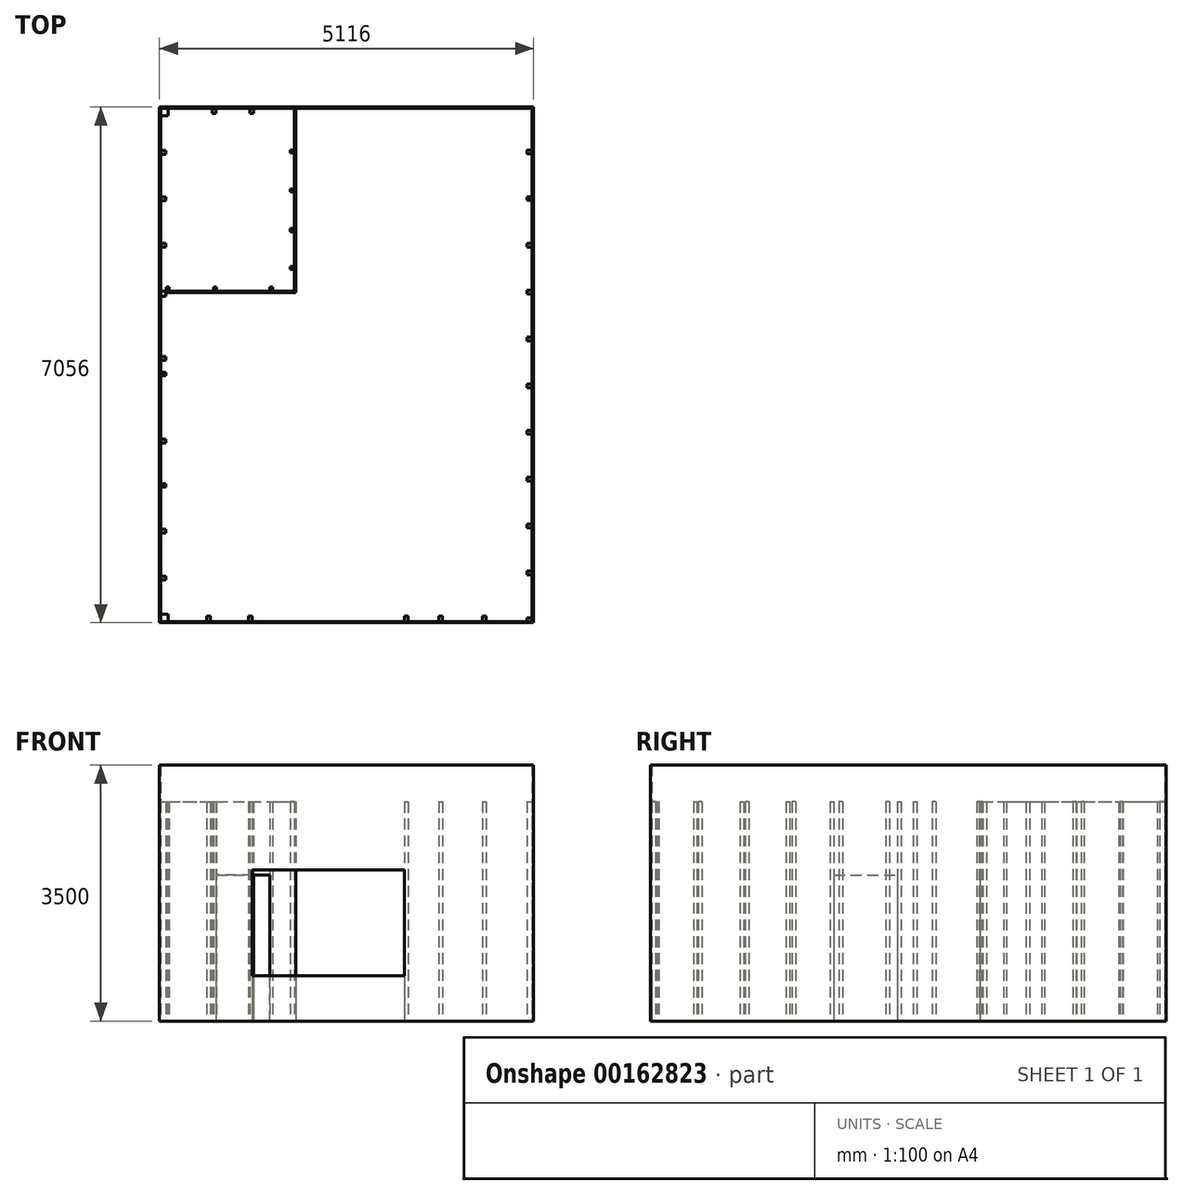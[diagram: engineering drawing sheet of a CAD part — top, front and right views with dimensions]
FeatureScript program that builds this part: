
annotation { "Feature Type Name" : "Feature", "Feature Type Description" : "" }
export const myFeature = defineFeature(function(context is Context, id is Id, definition is map)
    precondition{}
    {
        {
            assignVariable(context, id + "F0", {"name" : "Wys_zewnetrznych", "anyValue" : 3500});
        }
        {
            assignVariable(context, id + "F1", {"name" : "wys_parter", "anyValue" : 3000});
        }
        {
            var Q0;
            Q0=qCreatedBy(makeId("Top.planeOp"),FACE);
            var sketch = newSketch(context, id + "F2", { "sketchPlane" : qUnion([Q0])});
            skLineSegment(sketch, "E0", {"start": v(0, 0) * mm, "end": v(5080, 0) * mm});
            skLineSegment(sketch, "E1", {"start": v(0, 0) * mm, "end": v(0, 4500) * mm});
            skLineSegment(sketch, "E2", {"start": v(0, 4500) * mm, "end": v(1830, 4500) * mm});
            skLineSegment(sketch, "E3", {"start": v(1830, 4500) * mm, "end": v(1830, 7020) * mm});
            skLineSegment(sketch, "E4", {"start": v(1830, 7020) * mm, "end": v(5080, 7020) * mm});
            skLineSegment(sketch, "E5", {"start": v(5080, 7020) * mm, "end": v(5080, 0) * mm});
            skLineSegment(sketch, "E6", {"start": v(0, 4500) * mm, "end": v(0, 7020) * mm});
            skLineSegment(sketch, "E7", {"start": v(0, 7020) * mm, "end": v(1830, 7020) * mm});
            skLineSegment(sketch, "E8.bottom", {"start": v(5080, 0) * mm, "end": v(5010, 0) * mm});
            skLineSegment(sketch, "E8.top", {"start": v(5080, 50) * mm, "end": v(5010, 50) * mm});
            skLineSegment(sketch, "E8.left", {"start": v(5080, 0) * mm, "end": v(5080, 50) * mm});
            skLineSegment(sketch, "E8.right", {"start": v(5010, 0) * mm, "end": v(5010, 50) * mm});
            skLineSegment(sketch, "E9.0.1.0", {"start": v(5010, 640) * mm, "end": v(5010, 690) * mm});
            skLineSegment(sketch, "E9.0.1.1", {"start": v(5080, 690) * mm, "end": v(5010, 690) * mm});
            skLineSegment(sketch, "E9.0.1.2", {"start": v(5080, 640) * mm, "end": v(5080, 690) * mm});
            skLineSegment(sketch, "E9.0.1.3", {"start": v(5080, 640) * mm, "end": v(5010, 640) * mm});
            skLineSegment(sketch, "E9.0.2.0", {"start": v(5010, 1280) * mm, "end": v(5010, 1330) * mm});
            skLineSegment(sketch, "E9.0.2.1", {"start": v(5080, 1330) * mm, "end": v(5010, 1330) * mm});
            skLineSegment(sketch, "E9.0.2.2", {"start": v(5080, 1280) * mm, "end": v(5080, 1330) * mm});
            skLineSegment(sketch, "E9.0.2.3", {"start": v(5080, 1280) * mm, "end": v(5010, 1280) * mm});
            skLineSegment(sketch, "E9.0.3.0", {"start": v(5010, 1920) * mm, "end": v(5010, 1970) * mm});
            skLineSegment(sketch, "E9.0.3.1", {"start": v(5080, 1970) * mm, "end": v(5010, 1970) * mm});
            skLineSegment(sketch, "E9.0.3.2", {"start": v(5080, 1920) * mm, "end": v(5080, 1970) * mm});
            skLineSegment(sketch, "E9.0.3.3", {"start": v(5080, 1920) * mm, "end": v(5010, 1920) * mm});
            skLineSegment(sketch, "E9.0.4.0", {"start": v(5010, 2560) * mm, "end": v(5010, 2610) * mm});
            skLineSegment(sketch, "E9.0.4.1", {"start": v(5080, 2610) * mm, "end": v(5010, 2610) * mm});
            skLineSegment(sketch, "E9.0.4.2", {"start": v(5080, 2560) * mm, "end": v(5080, 2610) * mm});
            skLineSegment(sketch, "E9.0.4.3", {"start": v(5080, 2560) * mm, "end": v(5010, 2560) * mm});
            skLineSegment(sketch, "E9.0.5.0", {"start": v(5010, 3200) * mm, "end": v(5010, 3250) * mm});
            skLineSegment(sketch, "E9.0.5.1", {"start": v(5080, 3250) * mm, "end": v(5010, 3250) * mm});
            skLineSegment(sketch, "E9.0.5.2", {"start": v(5080, 3200) * mm, "end": v(5080, 3250) * mm});
            skLineSegment(sketch, "E9.0.5.3", {"start": v(5080, 3200) * mm, "end": v(5010, 3200) * mm});
            skLineSegment(sketch, "E9.0.6.0", {"start": v(5010, 3840) * mm, "end": v(5010, 3890) * mm});
            skLineSegment(sketch, "E9.0.6.1", {"start": v(5080, 3890) * mm, "end": v(5010, 3890) * mm});
            skLineSegment(sketch, "E9.0.6.2", {"start": v(5080, 3840) * mm, "end": v(5080, 3890) * mm});
            skLineSegment(sketch, "E9.0.6.3", {"start": v(5080, 3840) * mm, "end": v(5010, 3840) * mm});
            skLineSegment(sketch, "E9.0.7.0", {"start": v(5010, 4480) * mm, "end": v(5010, 4530) * mm});
            skLineSegment(sketch, "E9.0.7.1", {"start": v(5080, 4530) * mm, "end": v(5010, 4530) * mm});
            skLineSegment(sketch, "E9.0.7.2", {"start": v(5080, 4480) * mm, "end": v(5080, 4530) * mm});
            skLineSegment(sketch, "E9.0.7.3", {"start": v(5080, 4480) * mm, "end": v(5010, 4480) * mm});
            skLineSegment(sketch, "E9.0.8.0", {"start": v(5010, 5120) * mm, "end": v(5010, 5170) * mm});
            skLineSegment(sketch, "E9.0.8.1", {"start": v(5080, 5170) * mm, "end": v(5010, 5170) * mm});
            skLineSegment(sketch, "E9.0.8.2", {"start": v(5080, 5120) * mm, "end": v(5080, 5170) * mm});
            skLineSegment(sketch, "E9.0.8.3", {"start": v(5080, 5120) * mm, "end": v(5010, 5120) * mm});
            skLineSegment(sketch, "E9.0.9.0", {"start": v(5010, 5760) * mm, "end": v(5010, 5810) * mm});
            skLineSegment(sketch, "E9.0.9.1", {"start": v(5080, 5810) * mm, "end": v(5010, 5810) * mm});
            skLineSegment(sketch, "E9.0.9.2", {"start": v(5080, 5760) * mm, "end": v(5080, 5810) * mm});
            skLineSegment(sketch, "E9.0.9.3", {"start": v(5080, 5760) * mm, "end": v(5010, 5760) * mm});
            skLineSegment(sketch, "E9.0.10.0", {"start": v(5010, 6400) * mm, "end": v(5010, 6450) * mm});
            skLineSegment(sketch, "E9.0.10.1", {"start": v(5080, 6450) * mm, "end": v(5010, 6450) * mm});
            skLineSegment(sketch, "E9.0.10.2", {"start": v(5080, 6400) * mm, "end": v(5080, 6450) * mm});
            skLineSegment(sketch, "E9.0.10.3", {"start": v(5080, 6400) * mm, "end": v(5010, 6400) * mm});
            skLineSegment(sketch, "E9.direction1", {"start": v(5010, 0) * mm, "end": v(4985, 0) * mm, "construction": true});
            skLineSegment(sketch, "E9.direction2", {"start": v(5010, 0) * mm, "end": v(5010, 640) * mm, "construction": true});
            skLineSegment(sketch, "E10.bottom", {"start": v(4400, 0) * mm, "end": v(4450, 0) * mm});
            skLineSegment(sketch, "E10.top", {"start": v(4400, 70) * mm, "end": v(4450, 70) * mm});
            skLineSegment(sketch, "E10.left", {"start": v(4400, 0) * mm, "end": v(4400, 70) * mm});
            skLineSegment(sketch, "E10.right", {"start": v(4450, 0) * mm, "end": v(4450, 70) * mm});
            skLineSegment(sketch, "E11.bottom", {"start": v(3805, 0) * mm, "end": v(3855, 0) * mm});
            skLineSegment(sketch, "E11.top", {"start": v(3805, 70) * mm, "end": v(3855, 70) * mm});
            skLineSegment(sketch, "E11.left", {"start": v(3805, 0) * mm, "end": v(3805, 70) * mm});
            skLineSegment(sketch, "E11.right", {"start": v(3855, 0) * mm, "end": v(3855, 70) * mm});
            skLineSegment(sketch, "E12.bottom", {"start": v(3335, 0) * mm, "end": v(3385, 0) * mm});
            skLineSegment(sketch, "E12.top", {"start": v(3335, 70) * mm, "end": v(3385, 70) * mm});
            skLineSegment(sketch, "E12.left", {"start": v(3335, 0) * mm, "end": v(3335, 70) * mm});
            skLineSegment(sketch, "E12.right", {"start": v(3385, 0) * mm, "end": v(3385, 70) * mm});
            skLineSegment(sketch, "E13.bottom", {"start": v(0, 0) * mm, "end": v(100, 0) * mm});
            skLineSegment(sketch, "E13.top", {"start": v(0, 100) * mm, "end": v(100, 100) * mm});
            skLineSegment(sketch, "E13.left", {"start": v(0, 0) * mm, "end": v(0, 100) * mm});
            skLineSegment(sketch, "E13.right", {"start": v(100, 0) * mm, "end": v(100, 100) * mm});
            skLineSegment(sketch, "E14.bottom", {"start": v(627, 0) * mm, "end": v(677, 0) * mm});
            skLineSegment(sketch, "E14.top", {"start": v(627, 70) * mm, "end": v(677, 70) * mm});
            skLineSegment(sketch, "E14.left", {"start": v(627, 0) * mm, "end": v(627, 70) * mm});
            skLineSegment(sketch, "E14.right", {"start": v(677, 0) * mm, "end": v(677, 70) * mm});
            skLineSegment(sketch, "E15.bottom", {"start": v(1199, 0) * mm, "end": v(1249, 0) * mm});
            skLineSegment(sketch, "E15.top", {"start": v(1199, 70) * mm, "end": v(1249, 70) * mm});
            skLineSegment(sketch, "E15.left", {"start": v(1199, 0) * mm, "end": v(1199, 70) * mm});
            skLineSegment(sketch, "E15.right", {"start": v(1249, 0) * mm, "end": v(1249, 70) * mm});
            skText(sketch, "E16", { "text": "okno 620mm od podlogi\nwysokosc ok 1450", "fontName": "OpenSans-Regular.ttf"});
            skLineSegment(sketch, "E17.bottom", {"start": v(0, 571) * mm, "end": v(70, 571) * mm});
            skLineSegment(sketch, "E17.top", {"start": v(0, 621) * mm, "end": v(70, 621) * mm});
            skLineSegment(sketch, "E17.left", {"start": v(0, 571) * mm, "end": v(0, 621) * mm});
            skLineSegment(sketch, "E17.right", {"start": v(70, 571) * mm, "end": v(70, 621) * mm});
            skLineSegment(sketch, "E18.bottom", {"start": v(0, 1261) * mm, "end": v(70, 1261) * mm});
            skLineSegment(sketch, "E18.top", {"start": v(0, 1211) * mm, "end": v(70, 1211) * mm});
            skLineSegment(sketch, "E18.left", {"start": v(0, 1261) * mm, "end": v(0, 1211) * mm});
            skLineSegment(sketch, "E18.right", {"start": v(70, 1261) * mm, "end": v(70, 1211) * mm});
            skLineSegment(sketch, "E19.bottom", {"start": v(0, 1886) * mm, "end": v(70, 1886) * mm});
            skLineSegment(sketch, "E19.top", {"start": v(0, 1836) * mm, "end": v(70, 1836) * mm});
            skLineSegment(sketch, "E19.left", {"start": v(0, 1886) * mm, "end": v(0, 1836) * mm});
            skLineSegment(sketch, "E19.right", {"start": v(70, 1886) * mm, "end": v(70, 1836) * mm});
            skLineSegment(sketch, "E20.bottom", {"start": v(0, 2491) * mm, "end": v(70, 2491) * mm});
            skLineSegment(sketch, "E20.top", {"start": v(0, 2441) * mm, "end": v(70, 2441) * mm});
            skLineSegment(sketch, "E20.left", {"start": v(0, 2491) * mm, "end": v(0, 2441) * mm});
            skLineSegment(sketch, "E20.right", {"start": v(70, 2491) * mm, "end": v(70, 2441) * mm});
            skLineSegment(sketch, "E21.bottom", {"start": v(0, 3360) * mm, "end": v(70, 3360) * mm});
            skLineSegment(sketch, "E21.top", {"start": v(0, 3410) * mm, "end": v(70, 3410) * mm});
            skLineSegment(sketch, "E21.left", {"start": v(0, 3360) * mm, "end": v(0, 3410) * mm});
            skLineSegment(sketch, "E21.right", {"start": v(70, 3360) * mm, "end": v(70, 3410) * mm});
            skLineSegment(sketch, "E22.bottom", {"start": v(0, 3575) * mm, "end": v(70, 3575) * mm});
            skLineSegment(sketch, "E22.top", {"start": v(0, 3625) * mm, "end": v(70, 3625) * mm});
            skLineSegment(sketch, "E22.left", {"start": v(0, 3575) * mm, "end": v(0, 3625) * mm});
            skLineSegment(sketch, "E22.right", {"start": v(70, 3575) * mm, "end": v(70, 3625) * mm});
            skLineSegment(sketch, "E23.bottom", {"start": v(0, 4500) * mm, "end": v(70, 4500) * mm});
            skLineSegment(sketch, "E23.top", {"start": v(0, 4450) * mm, "end": v(70, 4450) * mm});
            skLineSegment(sketch, "E23.left", {"start": v(0, 4500) * mm, "end": v(0, 4450) * mm});
            skLineSegment(sketch, "E23.right", {"start": v(70, 4500) * mm, "end": v(70, 4450) * mm});
            skLineSegment(sketch, "E24.bottom", {"start": v(75, 4518) * mm, "end": v(115, 4518) * mm});
            skLineSegment(sketch, "E24.top", {"start": v(75, 4578) * mm, "end": v(115, 4578) * mm});
            skLineSegment(sketch, "E24.left", {"start": v(75, 4518) * mm, "end": v(75, 4578) * mm});
            skLineSegment(sketch, "E24.right", {"start": v(115, 4518) * mm, "end": v(115, 4578) * mm});
            skLineSegment(sketch, "E25.bottom", {"start": v(723, 4518) * mm, "end": v(763, 4518) * mm});
            skLineSegment(sketch, "E25.top", {"start": v(723, 4578) * mm, "end": v(763, 4578) * mm});
            skLineSegment(sketch, "E25.left", {"start": v(723, 4518) * mm, "end": v(723, 4578) * mm});
            skLineSegment(sketch, "E25.right", {"start": v(763, 4518) * mm, "end": v(763, 4578) * mm});
            skLineSegment(sketch, "E26.bottom", {"start": v(1490, 4518) * mm, "end": v(1530, 4518) * mm});
            skLineSegment(sketch, "E26.top", {"start": v(1490, 4578) * mm, "end": v(1530, 4578) * mm});
            skLineSegment(sketch, "E26.left", {"start": v(1490, 4518) * mm, "end": v(1490, 4578) * mm});
            skLineSegment(sketch, "E26.right", {"start": v(1530, 4518) * mm, "end": v(1530, 4578) * mm});
            skLineSegment(sketch, "E27.top", {"start": v(1775, 4578) * mm, "end": v(1815, 4578) * mm});
            skLineSegment(sketch, "E27.left", {"start": v(1775, 4518) * mm, "end": v(1775, 4578) * mm});
            skLineSegment(sketch, "E27.right", {"start": v(1815, 4518) * mm, "end": v(1815, 4578) * mm});
            skLineSegment(sketch, "E28.bottom", {"start": v(1830, 4816) * mm, "end": v(1770, 4816) * mm});
            skLineSegment(sketch, "E28.top", {"start": v(1830, 4856) * mm, "end": v(1770, 4856) * mm});
            skLineSegment(sketch, "E28.left", {"start": v(1830, 4816) * mm, "end": v(1830, 4856) * mm});
            skLineSegment(sketch, "E28.right", {"start": v(1770, 4816) * mm, "end": v(1770, 4856) * mm});
            skLineSegment(sketch, "E29.bottom", {"start": v(1830, 5334) * mm, "end": v(1770, 5334) * mm});
            skLineSegment(sketch, "E29.top", {"start": v(1830, 5374) * mm, "end": v(1770, 5374) * mm});
            skLineSegment(sketch, "E29.left", {"start": v(1830, 5334) * mm, "end": v(1830, 5374) * mm});
            skLineSegment(sketch, "E29.right", {"start": v(1770, 5334) * mm, "end": v(1770, 5374) * mm});
            skLineSegment(sketch, "E30.bottom", {"start": v(1830, 5916) * mm, "end": v(1770, 5916) * mm});
            skLineSegment(sketch, "E30.top", {"start": v(1830, 5876) * mm, "end": v(1770, 5876) * mm});
            skLineSegment(sketch, "E30.left", {"start": v(1830, 5916) * mm, "end": v(1830, 5876) * mm});
            skLineSegment(sketch, "E30.right", {"start": v(1770, 5916) * mm, "end": v(1770, 5876) * mm});
            skLineSegment(sketch, "E31.bottom", {"start": v(1830, 6408) * mm, "end": v(1770, 6408) * mm});
            skLineSegment(sketch, "E31.top", {"start": v(1830, 6448) * mm, "end": v(1770, 6448) * mm});
            skLineSegment(sketch, "E31.left", {"start": v(1830, 6408) * mm, "end": v(1830, 6448) * mm});
            skLineSegment(sketch, "E31.right", {"start": v(1770, 6408) * mm, "end": v(1770, 6448) * mm});
            skLineSegment(sketch, "E32.bottom", {"start": v(0, 7020) * mm, "end": v(100, 7020) * mm});
            skLineSegment(sketch, "E32.top", {"start": v(0, 6920) * mm, "end": v(100, 6920) * mm});
            skLineSegment(sketch, "E32.left", {"start": v(0, 7020) * mm, "end": v(0, 6920) * mm});
            skLineSegment(sketch, "E32.right", {"start": v(100, 7020) * mm, "end": v(100, 6920) * mm});
            skLineSegment(sketch, "E33.bottom", {"start": v(704, 7020) * mm, "end": v(754, 7020) * mm});
            skLineSegment(sketch, "E33.top", {"start": v(704, 6950) * mm, "end": v(754, 6950) * mm});
            skLineSegment(sketch, "E33.left", {"start": v(704, 7020) * mm, "end": v(704, 6950) * mm});
            skLineSegment(sketch, "E33.right", {"start": v(754, 7020) * mm, "end": v(754, 6950) * mm});
            skLineSegment(sketch, "E34.bottom", {"start": v(1269, 7020) * mm, "end": v(1219, 7020) * mm});
            skLineSegment(sketch, "E34.top", {"start": v(1269, 6950) * mm, "end": v(1219, 6950) * mm});
            skLineSegment(sketch, "E34.left", {"start": v(1269, 7020) * mm, "end": v(1269, 6950) * mm});
            skLineSegment(sketch, "E34.right", {"start": v(1219, 7020) * mm, "end": v(1219, 6950) * mm});
            skLineSegment(sketch, "E35.bottom", {"start": v(0, 6442) * mm, "end": v(70, 6442) * mm});
            skLineSegment(sketch, "E35.top", {"start": v(0, 6392) * mm, "end": v(70, 6392) * mm});
            skLineSegment(sketch, "E35.left", {"start": v(0, 6442) * mm, "end": v(0, 6392) * mm});
            skLineSegment(sketch, "E35.right", {"start": v(70, 6442) * mm, "end": v(70, 6392) * mm});
            skLineSegment(sketch, "E36.bottom", {"start": v(0, 5759) * mm, "end": v(70, 5759) * mm});
            skLineSegment(sketch, "E36.top", {"start": v(0, 5809) * mm, "end": v(70, 5809) * mm});
            skLineSegment(sketch, "E36.left", {"start": v(0, 5759) * mm, "end": v(0, 5809) * mm});
            skLineSegment(sketch, "E36.right", {"start": v(70, 5759) * mm, "end": v(70, 5809) * mm});
            skLineSegment(sketch, "E37.bottom", {"start": v(0, 5120) * mm, "end": v(70, 5120) * mm});
            skLineSegment(sketch, "E37.top", {"start": v(0, 5170) * mm, "end": v(70, 5170) * mm});
            skLineSegment(sketch, "E37.left", {"start": v(0, 5120) * mm, "end": v(0, 5170) * mm});
            skLineSegment(sketch, "E37.right", {"start": v(70, 5120) * mm, "end": v(70, 5170) * mm});
            skLineSegment(sketch, "E38", {"start": v(1775, 4518) * mm, "end": v(1815, 4518) * mm});
            skPoint(sketch, "E38.startSnap0", {"position": v(1510, 4518) * mm});
            skPoint(sketch, "E39.orphan", {"position": v(1775, 4546.29) * mm});
            skPoint(sketch, "E40.orphan", {"position": v(1815, 4518) * mm});
            skPoint(sketch, "E41.orphan", {"position": v(1815, 4550.5) * mm});
            const initialGuessF2  = {"E16": [1.86616, -0.28119, 1, 0, 0.10051]};
            skSetInitialGuess(sketch, initialGuessF2);
            skSolve(sketch);
        }
        {
            var Q0;
            {var subQ39=sQuery(id+"F2.wireOp",EDGE,"E4");Q0=makeQuery(id+"F2.imprint","IMPRINT",FACE,{"disambiguationData":[TD([[makeQuery(id+"F2.imprint","IMPRINT",EDGE,{"derivedFrom":subQ39}),-1.0]])]});}
            var sketch = newSketch(context, id + "F3", { "sketchPlane" : qUnion([Q0])});
            skPoint(sketch, "E42.orphan", {"position": v(0, 7021.81) * mm});
            skLineSegment(sketch, "E43.0", {"start": v(0, 7020) * mm, "end": v(1830, 7020) * mm});
            skLineSegment(sketch, "E43.1", {"start": v(1830, 7020) * mm, "end": v(5080, 7020) * mm});
            skLineSegment(sketch, "E43.2", {"start": v(0, 4500) * mm, "end": v(0, 7020) * mm});
            skLineSegment(sketch, "E43.3", {"start": v(0, 0) * mm, "end": v(0, 4500) * mm});
            skLineSegment(sketch, "E43.4", {"start": v(0, 0) * mm, "end": v(5080, 0) * mm});
            skLineSegment(sketch, "E43.5", {"start": v(5080, 7020) * mm, "end": v(5080, 0) * mm});
            skLineSegment(sketch, "E44.0", {"start": v(-18, 7038) * mm, "end": v(1830, 7038) * mm});
            skLineSegment(sketch, "E44.1", {"start": v(5098, 7038) * mm, "end": v(5098, -18) * mm});
            skLineSegment(sketch, "E44.2", {"start": v(-18, -18) * mm, "end": v(5098, -18) * mm});
            skLineSegment(sketch, "E44.3", {"start": v(1830, 7038) * mm, "end": v(5098, 7038) * mm});
            skLineSegment(sketch, "E44.4", {"start": v(-18, -18) * mm, "end": v(-18, 4500) * mm});
            skLineSegment(sketch, "E44.5", {"start": v(-18, 4500) * mm, "end": v(-18, 7038) * mm});
            skSolve(sketch);
        }
        {
            var Q0;
            Q0 = qSketchRegion(id + "F3", true);
            extrude(context, id + "F4", {"entities" : qUnion([Q0]), "depth" : (getVariable(context, 'Wys_zewnetrznych')) * mm});
        }
        {
            var Q0;
            {var subQ39=sQuery(id+"F2.wireOp",EDGE,"E4");Q0=makeQuery(id+"F2.imprint","IMPRINT",FACE,{"disambiguationData":[TD([[makeQuery(id+"F2.imprint","IMPRINT",EDGE,{"derivedFrom":subQ39}),-1.0]])]});}
            var sketch = newSketch(context, id + "F5", { "sketchPlane" : qUnion([Q0])});
            skLineSegment(sketch, "E45.0", {"start": v(0, 4500) * mm, "end": v(1830, 4500) * mm});
            skLineSegment(sketch, "E45.1", {"start": v(1830, 4518) * mm, "end": v(1830, 7020) * mm});
            skLineSegment(sketch, "E46.0", {"start": v(0, 4518) * mm, "end": v(1830, 4518) * mm});
            skLineSegment(sketch, "E47", {"start": v(0, 4500) * mm, "end": v(0, 4518) * mm});
            skLineSegment(sketch, "E48.0", {"start": v(1848, 4500) * mm, "end": v(1848, 7020) * mm});
            skLineSegment(sketch, "E49", {"start": v(1830, 4500) * mm, "end": v(1848, 4500) * mm});
            skLineSegment(sketch, "E50", {"start": v(1830, 7020) * mm, "end": v(1848, 7020) * mm});
            skPoint(sketch, "E51.orphan", {"position": v(1830, 4500) * mm});
            skSolve(sketch);
        }
        {
            var Q0;
            Q0 = qSketchRegion(id + "F5", true);
            extrude(context, id + "F6", {"entities" : qUnion([Q0]), "operationType" : NewBodyOperationType.ADD, "depth" : (getVariable(context, 'wys_parter')) * mm});
        }
        {
            var Q0;
            {var subQ3=sQuery(id+"F2.wireOp",EDGE,"E23.top");Q0=makeQuery(id+"F2.imprint","IMPRINT",FACE,{"disambiguationData":[TD([[makeQuery(id+"F2.imprint","IMPRINT",EDGE,{"derivedFrom":subQ3}),1.0]])]});}
            var Q1;
            {var subQ0=sQuery(id+"F2.wireOp",EDGE,"E22.bottom");Q1=makeQuery(id+"F2.imprint","IMPRINT",FACE,{"disambiguationData":[TD([[makeQuery(id+"F2.imprint","IMPRINT",EDGE,{"derivedFrom":subQ0}),1.0]])]});}
            var Q2;
            {var subQ0=sQuery(id+"F2.wireOp",EDGE,"E21.bottom");Q2=makeQuery(id+"F2.imprint","IMPRINT",FACE,{"disambiguationData":[TD([[makeQuery(id+"F2.imprint","IMPRINT",EDGE,{"derivedFrom":subQ0}),1.0]])]});}
            var Q3;
            {var subQ0=sQuery(id+"F2.wireOp",EDGE,"E20.bottom");Q3=makeQuery(id+"F2.imprint","IMPRINT",FACE,{"disambiguationData":[TD([[makeQuery(id+"F2.imprint","IMPRINT",EDGE,{"derivedFrom":subQ0}),-1.0]])]});}
            var Q4;
            {var subQ0=sQuery(id+"F2.wireOp",EDGE,"E19.bottom");Q4=makeQuery(id+"F2.imprint","IMPRINT",FACE,{"disambiguationData":[TD([[makeQuery(id+"F2.imprint","IMPRINT",EDGE,{"derivedFrom":subQ0}),-1.0]])]});}
            var Q5;
            {var subQ0=sQuery(id+"F2.wireOp",EDGE,"E18.bottom");Q5=makeQuery(id+"F2.imprint","IMPRINT",FACE,{"disambiguationData":[TD([[makeQuery(id+"F2.imprint","IMPRINT",EDGE,{"derivedFrom":subQ0}),-1.0]])]});}
            var Q6;
            {var subQ0=sQuery(id+"F2.wireOp",EDGE,"E17.bottom");Q6=makeQuery(id+"F2.imprint","IMPRINT",FACE,{"disambiguationData":[TD([[makeQuery(id+"F2.imprint","IMPRINT",EDGE,{"derivedFrom":subQ0}),1.0]])]});}
            var Q7;
            {var subQ4=sQuery(id+"F2.wireOp",EDGE,"E13.top");Q7=makeQuery(id+"F2.imprint","IMPRINT",FACE,{"disambiguationData":[TD([[makeQuery(id+"F2.imprint","IMPRINT",EDGE,{"derivedFrom":subQ4}),-1.0]])]});}
            var Q8;
            Q8=makeQuery(id+"F2.imprint","IMPRINT",FACE,{"disambiguationData":[TD([[makeQuery(id+"F2.imprint","IMPRINT",EDGE,{"derivedFrom":sQuery(id+"F2.wireOp",EDGE,"E14.top")}),-1.0]])]});
            var Q9;
            Q9=makeQuery(id+"F2.imprint","IMPRINT",FACE,{"disambiguationData":[TD([[makeQuery(id+"F2.imprint","IMPRINT",EDGE,{"derivedFrom":sQuery(id+"F2.wireOp",EDGE,"E15.top")}),-1.0]])]});
            var Q10;
            Q10=makeQuery(id+"F2.imprint","IMPRINT",FACE,{"disambiguationData":[TD([[makeQuery(id+"F2.imprint","IMPRINT",EDGE,{"derivedFrom":sQuery(id+"F2.wireOp",EDGE,"E12.top")}),-1.0]])]});
            var Q11;
            Q11=makeQuery(id+"F2.imprint","IMPRINT",FACE,{"disambiguationData":[TD([[makeQuery(id+"F2.imprint","IMPRINT",EDGE,{"derivedFrom":sQuery(id+"F2.wireOp",EDGE,"E11.top")}),-1.0]])]});
            var Q12;
            Q12=makeQuery(id+"F2.imprint","IMPRINT",FACE,{"disambiguationData":[TD([[makeQuery(id+"F2.imprint","IMPRINT",EDGE,{"derivedFrom":sQuery(id+"F2.wireOp",EDGE,"E10.top")}),-1.0]])]});
            var Q13;
            {var subQ4=sQuery(id+"F2.wireOp",EDGE,"E8.top");Q13=makeQuery(id+"F2.imprint","IMPRINT",FACE,{"disambiguationData":[TD([[makeQuery(id+"F2.imprint","IMPRINT",EDGE,{"derivedFrom":subQ4}),1.0]])]});}
            var Q14;
            Q14=makeQuery(id+"F2.imprint","IMPRINT",FACE,{"disambiguationData":[TD([[makeQuery(id+"F2.imprint","IMPRINT",EDGE,{"derivedFrom":sQuery(id+"F2.wireOp",EDGE,"E9.0.1.0")}),-1.0]])]});
            var Q15;
            Q15=makeQuery(id+"F2.imprint","IMPRINT",FACE,{"disambiguationData":[TD([[makeQuery(id+"F2.imprint","IMPRINT",EDGE,{"derivedFrom":sQuery(id+"F2.wireOp",EDGE,"E9.0.2.0")}),-1.0]])]});
            var Q16;
            Q16=makeQuery(id+"F2.imprint","IMPRINT",FACE,{"disambiguationData":[TD([[makeQuery(id+"F2.imprint","IMPRINT",EDGE,{"derivedFrom":sQuery(id+"F2.wireOp",EDGE,"E9.0.3.0")}),-1.0]])]});
            var Q17;
            Q17=makeQuery(id+"F2.imprint","IMPRINT",FACE,{"disambiguationData":[TD([[makeQuery(id+"F2.imprint","IMPRINT",EDGE,{"derivedFrom":sQuery(id+"F2.wireOp",EDGE,"E9.0.4.0")}),-1.0]])]});
            var Q18;
            Q18=makeQuery(id+"F2.imprint","IMPRINT",FACE,{"disambiguationData":[TD([[makeQuery(id+"F2.imprint","IMPRINT",EDGE,{"derivedFrom":sQuery(id+"F2.wireOp",EDGE,"E9.0.5.0")}),-1.0]])]});
            var Q19;
            Q19=makeQuery(id+"F2.imprint","IMPRINT",FACE,{"disambiguationData":[TD([[makeQuery(id+"F2.imprint","IMPRINT",EDGE,{"derivedFrom":sQuery(id+"F2.wireOp",EDGE,"E9.0.6.0")}),-1.0]])]});
            var Q20;
            Q20=makeQuery(id+"F2.imprint","IMPRINT",FACE,{"disambiguationData":[TD([[makeQuery(id+"F2.imprint","IMPRINT",EDGE,{"derivedFrom":sQuery(id+"F2.wireOp",EDGE,"E9.0.7.0")}),-1.0]])]});
            var Q21;
            Q21=makeQuery(id+"F2.imprint","IMPRINT",FACE,{"disambiguationData":[TD([[makeQuery(id+"F2.imprint","IMPRINT",EDGE,{"derivedFrom":sQuery(id+"F2.wireOp",EDGE,"E9.0.8.0")}),-1.0]])]});
            var Q22;
            Q22=makeQuery(id+"F2.imprint","IMPRINT",FACE,{"disambiguationData":[TD([[makeQuery(id+"F2.imprint","IMPRINT",EDGE,{"derivedFrom":sQuery(id+"F2.wireOp",EDGE,"E9.0.9.0")}),-1.0]])]});
            var Q23;
            Q23=makeQuery(id+"F2.imprint","IMPRINT",FACE,{"disambiguationData":[TD([[makeQuery(id+"F2.imprint","IMPRINT",EDGE,{"derivedFrom":sQuery(id+"F2.wireOp",EDGE,"E9.0.10.0")}),-1.0]])]});
            var Q24;
            {var subQ0=sQuery(id+"F2.wireOp",EDGE,"E32.top");Q24=makeQuery(id+"F2.imprint","IMPRINT",FACE,{"disambiguationData":[TD([[makeQuery(id+"F2.imprint","IMPRINT",EDGE,{"derivedFrom":subQ0}),1.0]])]});}
            var Q25;
            Q25=makeQuery(id+"F2.imprint","IMPRINT",FACE,{"disambiguationData":[TD([[makeQuery(id+"F2.imprint","IMPRINT",EDGE,{"derivedFrom":sQuery(id+"F2.wireOp",EDGE,"E33.top")}),1.0]])]});
            var Q26;
            Q26=makeQuery(id+"F2.imprint","IMPRINT",FACE,{"disambiguationData":[TD([[makeQuery(id+"F2.imprint","IMPRINT",EDGE,{"derivedFrom":sQuery(id+"F2.wireOp",EDGE,"E34.top")}),-1.0]])]});
            var Q27;
            {var subQ2=sQuery(id+"F2.wireOp",EDGE,"E31.bottom");Q27=makeQuery(id+"F2.imprint","IMPRINT",FACE,{"disambiguationData":[TD([[makeQuery(id+"F2.imprint","IMPRINT",EDGE,{"derivedFrom":subQ2}),-1.0]])]});}
            var Q28;
            {var subQ0=sQuery(id+"F2.wireOp",EDGE,"E30.bottom");Q28=makeQuery(id+"F2.imprint","IMPRINT",FACE,{"disambiguationData":[TD([[makeQuery(id+"F2.imprint","IMPRINT",EDGE,{"derivedFrom":subQ0}),1.0]])]});}
            var Q29;
            {var subQ2=sQuery(id+"F2.wireOp",EDGE,"E29.bottom");Q29=makeQuery(id+"F2.imprint","IMPRINT",FACE,{"disambiguationData":[TD([[makeQuery(id+"F2.imprint","IMPRINT",EDGE,{"derivedFrom":subQ2}),-1.0]])]});}
            var Q30;
            {var subQ0=sQuery(id+"F2.wireOp",EDGE,"E28.bottom");Q30=makeQuery(id+"F2.imprint","IMPRINT",FACE,{"disambiguationData":[TD([[makeQuery(id+"F2.imprint","IMPRINT",EDGE,{"derivedFrom":subQ0}),-1.0]])]});}
            var Q31;
            {var subQ0=sQuery(id+"F2.wireOp",EDGE,"E35.bottom");Q31=makeQuery(id+"F2.imprint","IMPRINT",FACE,{"disambiguationData":[TD([[makeQuery(id+"F2.imprint","IMPRINT",EDGE,{"derivedFrom":subQ0}),-1.0]])]});}
            var Q32;
            {var subQ0=sQuery(id+"F2.wireOp",EDGE,"E36.bottom");Q32=makeQuery(id+"F2.imprint","IMPRINT",FACE,{"disambiguationData":[TD([[makeQuery(id+"F2.imprint","IMPRINT",EDGE,{"derivedFrom":subQ0}),1.0]])]});}
            var Q33;
            {var subQ2=sQuery(id+"F2.wireOp",EDGE,"E37.bottom");Q33=makeQuery(id+"F2.imprint","IMPRINT",FACE,{"disambiguationData":[TD([[makeQuery(id+"F2.imprint","IMPRINT",EDGE,{"derivedFrom":subQ2}),1.0]])]});}
            var Q34;
            Q34=makeQuery(id+"F2.imprint","IMPRINT",FACE,{"disambiguationData":[TD([[makeQuery(id+"F2.imprint","IMPRINT",EDGE,{"derivedFrom":sQuery(id+"F2.wireOp",EDGE,"E24.bottom")}),1.0]])]});
            var Q35;
            Q35=makeQuery(id+"F2.imprint","IMPRINT",FACE,{"disambiguationData":[TD([[makeQuery(id+"F2.imprint","IMPRINT",EDGE,{"derivedFrom":sQuery(id+"F2.wireOp",EDGE,"E25.bottom")}),1.0]])]});
            var Q36;
            Q36=makeQuery(id+"F2.imprint","IMPRINT",FACE,{"disambiguationData":[TD([[makeQuery(id+"F2.imprint","IMPRINT",EDGE,{"derivedFrom":sQuery(id+"F2.wireOp",EDGE,"E26.bottom")}),1.0]])]});
            var Q37;
            Q37=makeQuery(id+"F2.imprint","IMPRINT",FACE,{"disambiguationData":[TD([[makeQuery(id+"F2.imprint","IMPRINT",EDGE,{"derivedFrom":sQuery(id+"F2.wireOp",EDGE,"E27.bottom")}),1.0]])]});
            extrude(context, id + "F7", {"entities" : qUnion([Q0, Q1, Q2, Q3, Q4, Q5, Q6, Q7, Q8, Q9, Q10, Q11, Q12, Q13, Q14, Q15, Q16, Q17, Q18, Q19, Q20, Q21, Q22, Q23, Q24, Q25, Q26, Q27, Q28, Q29, Q30, Q31, Q32, Q33, Q34, Q35, Q36, Q37]), "operationType" : NewBodyOperationType.ADD, "depth" : (getVariable(context, 'wys_parter')) * mm});
        }
        {
            var Q0;
            Q0=makeQuery(id+"F4.opExtrude","SWEPT_FACE",FACE,{"disambiguationData":[OSD([sQuery(id+"F3.wireOp",EDGE,"E44.2")])]});
            var sketch = newSketch(context, id + "F8", { "sketchPlane" : qUnion([Q0])});
            skLineSegment(sketch, "E52.0", {"start": v(1249, 2070) * mm, "end": v(1249, 620) * mm});
            skLineSegment(sketch, "E52.1", {"start": v(3335, 2070) * mm, "end": v(3335, 620) * mm});
            skLineSegment(sketch, "E53", {"start": v(1249, 620) * mm, "end": v(3335, 620) * mm});
            skLineSegment(sketch, "E54", {"start": v(1249, 2070) * mm, "end": v(3335, 2070) * mm});
            skSolve(sketch);
        }
        {
            var Q0;
            Q0=makeQuery(id+"F8.imprint","IMPRINT",FACE,{"disambiguationData":[TD([[makeQuery(id+"F8.imprint","IMPRINT",EDGE,{"derivedFrom":sQuery(id+"F8.wireOp",EDGE,"E52.0")}),1.0]])]});
            extrude(context, id + "F9", {"entities" : qUnion([Q0]), "operationType" : NewBodyOperationType.REMOVE, "endBound" : BoundingType.UP_TO_NEXT, "oppositeDirection" : true, "depth" : 25 * mm});
        }
        {
            var Q0;
            Q0=makeQuery(id+"F4.opExtrude","SWEPT_FACE",FACE,{"disambiguationData":[OSD([sQuery(id+"F3.wireOp",EDGE,"E43.2"),sQuery(id+"F3.wireOp",EDGE,"E43.3")])]});
            var sketch = newSketch(context, id + "F10", { "sketchPlane" : qUnion([Q0])});
            skLineSegment(sketch, "E55.0", {"start": v(3360, 2000) * mm, "end": v(3360, 0) * mm});
            skLineSegment(sketch, "E55.1", {"start": v(2491, 2000) * mm, "end": v(2491, 0) * mm});
            skLineSegment(sketch, "E56", {"start": v(2491, 2000) * mm, "end": v(3360, 2000) * mm});
            skLineSegment(sketch, "E57", {"start": v(2491, 0) * mm, "end": v(3360, 0) * mm});
            skSolve(sketch);
        }
        {
            var Q0;
            Q0=makeQuery(id+"F10.imprint","IMPRINT",FACE,{"disambiguationData":[TD([[makeQuery(id+"F10.imprint","IMPRINT",EDGE,{"derivedFrom":sQuery(id+"F10.wireOp",EDGE,"E55.0")}),-1.0]])]});
            extrude(context, id + "F11", {"entities" : qUnion([Q0]), "operationType" : NewBodyOperationType.REMOVE, "endBound" : BoundingType.UP_TO_NEXT, "oppositeDirection" : true, "depth" : 25 * mm});
        }
        {
            var Q0;
            {var subQ0=sQuery(id+"F2.wireOp",EDGE,"E25.right");var subQ8=sQuery(id+"F5.wireOp",EDGE,"E46.0");Q0=makeQuery(id+"F7.boolean.opBoolean","SPLIT",FACE,{"disambiguationData":[TD([makeQuery(id+"F7.opExtrude","SWEPT_FACE",FACE,{"disambiguationData":[OSD([subQ0])]})])],"derivedFrom":makeQuery(id+"F6.opExtrude","SWEPT_FACE",FACE,{"disambiguationData":[OSD([subQ8])]})});}
            var sketch = newSketch(context, id + "F12", { "sketchPlane" : qUnion([Q0])});
            skLineSegment(sketch, "E58.0", {"start": v(-1490, 2000) * mm, "end": v(-1490, 0) * mm});
            skLineSegment(sketch, "E58.1", {"start": v(-763, 2000) * mm, "end": v(-763, 0) * mm});
            skLineSegment(sketch, "E59", {"start": v(-1490, 0) * mm, "end": v(-763, 0) * mm});
            skLineSegment(sketch, "E60", {"start": v(-1490, 2000) * mm, "end": v(-763, 2000) * mm});
            skPoint(sketch, "E61.orphan", {"position": v(-1490, 3000) * mm});
            skPoint(sketch, "E62.orphan", {"position": v(-763, 3000) * mm});
            skSolve(sketch);
        }
        {
            var Q0;
            Q0=makeQuery(id+"F12.imprint","IMPRINT",FACE,{"disambiguationData":[TD([[makeQuery(id+"F12.imprint","IMPRINT",EDGE,{"derivedFrom":sQuery(id+"F12.wireOp",EDGE,"E58.0")}),1.0]])]});
            extrude(context, id + "F13", {"entities" : qUnion([Q0]), "operationType" : NewBodyOperationType.REMOVE, "endBound" : BoundingType.UP_TO_NEXT, "oppositeDirection" : true, "depth" : 25 * mm});
        }
    });
